# Revit family: TV-121
name_source: partatom
category: Plumbing Fixtures
revit_build: Autodesk Revit 2014 (Build: 20130308_1515(x64)
units: mm (PartAtom-declared; Revit-internal decimal feet)

## types (1)
- TV-121
    CW Connection = No
    Certification = http://www.helvex.com.mx
    Chrome = Brass Chromed
    Connection = ½" - 14 NPSM
    Description = Single Faucet Economizer To Wall Closing And Antibacterial Coating
    Documentation = http://www.helvex.com.mx
    Features = Automatic Closure, Activation Time Adjustable, Button With Antibacterial Coating, Closing Time Adjustable From 5 To 13 Seconds
    Instructive = http://www.helvex.com.mx
    Manufacturer = HELVEX
    Max. Water Flow = 2.1 gal/min
    Max. Working Pressure = 85.3 psi
    Min. Working Pressure = 14.2 psi
    Model = TV-121
    Support Base Diameter = 2"
    Total Length = 8"
    Type Comments = Special Products
    URL = http://www.helvex.com.mx

## geometry (parser evidence)
native form markers: Sweep x3
no freeform markers — native parametric forms only
